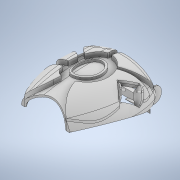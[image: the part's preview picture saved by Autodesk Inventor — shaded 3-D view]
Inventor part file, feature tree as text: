
AUTODESK INVENTOR PART (.ipt)
format: ipt  version: 2022 (Build 260153000, 153)  size: 2,761,216 bytes
history: native  units: mm
features: extrude x44, sketch x21, other x16, fillet x6, loft x1, shell x1, projected_geometry x1
ambient origin geometry x8: Origin, YZ Plane, XZ Plane, XY Plane, X Axis, Y Axis, Z Axis, Center Point
bodies: Body1 (feature_tree)
feature tree (90):
  other  "솔리드2"
  sketch  "스케치3"
  other  "작업 평면1"
  other  "작업 평면3"
  other  "작업 평면4"
  sketch  "스케치9"
  sketch  "스케치10"
  loft  "로프트1"
  shell  "쉘1"  Thickness=20.0mm
  fillet  "모깎기2"  [1 undecoded]
  extrude  "돌출3"  Depth=40.0mm
  extrude  "돌출5"  Depth=55.0mm
  extrude  "돌출6"  Depth=40.0mm
  sketch  "스케치21"
  sketch  "스케치22"
  sketch  "스케치23"
  sketch  "스케치24"
  extrude  "돌출9"  Depth=45.0mm
  extrude  "돌출10"  Depth=25.0mm
  extrude  "돌출11"  TaperAngle=0.0deg  [1 undecoded]
  fillet  "모깎기3"  [1 undecoded]
  other  "작업 평면9"
  sketch  "스케치28"
  other  "작업 평면11"
  extrude  "돌출12"  TaperAngle=0.0deg  [1 undecoded]
  fillet  "모깎기4"  Radius=5.0mm
  other  "작업 평면13"
  other  "작업 평면14"
  extrude  "돌출14"  Depth=110.605575mm
  extrude  "돌출15"  Depth=20.0mm
  sketch  "스케치32"
  extrude  "돌출16"  Depth=20.0mm
  extrude  "돌출17"  Depth=20.0mm
  fillet  "모깎기5"  Radius=20.0mm
  other  "작업 평면15"
  sketch  "스케치34"
  extrude  "돌출18"  Depth=20.0mm
  extrude  "돌출19"  Depth=1.677mm
  extrude  "돌출20"  Depth=1.677mm
  extrude  "돌출21"  Depth=1.677mm
  extrude  "돌출22"  Depth=1.677mm
  extrude  "돌출23"  Depth=88.385mm
  extrude  "돌출24"  Depth=44.1925mm
  extrude  "돌출25"  Depth=10.0mm
  extrude  "돌출26"  Depth=12.5mm
  extrude  "돌출27"  Depth=5.0mm TaperAngle=0.0deg
  extrude  "돌출28"  Depth=5.0mm TaperAngle=0.0deg
  sketch  "스케치35"
  sketch  "스케치36"
  extrude  "돌출29"  Depth=5.0mm TaperAngle=0.0deg
  extrude  "돌출30"  Depth=2.0mm
  other  "작업 평면16"
  sketch  "스케치37"
  extrude  "돌출31"  Depth=4.0mm TaperAngle=0.0deg
  extrude  "돌출32"  Depth=4.0mm TaperAngle=0.0deg
  extrude  "돌출33"  Depth=4.0mm TaperAngle=0.0deg
  extrude  "돌출34"  Depth=9.0mm
  extrude  "돌출35"  TaperAngle=0.0deg  [1 undecoded]
  extrude  "돌출36"  [1 undecoded]
  extrude  "돌출37"  Depth=50.0mm TaperAngle=0.0deg
  extrude  "돌출38"  Depth=2.0mm
  sketch  "스케치40"
  extrude  "돌출40"  Depth=30.0mm TaperAngle=30.0deg
  extrude  "돌출41"  Depth=6.108652mm
  extrude  "돌출42"  Depth=20.0mm
  other  "작업 평면17"
  sketch  "스케치42"
  extrude  "돌출43"  Depth=20.0mm
  extrude  "돌출44"  Depth=30.0mm TaperAngle=0.0deg
  extrude  "돌출45"  Depth=1.677mm
  extrude  "돌출46"  Depth=1.677mm
  other  "작업 평면18"
  extrude  "돌출47"  Depth=20.0mm TaperAngle=0.0deg
  extrude  "돌출48"  Depth=20.0mm
  extrude  "돌출49"  Depth=10.0mm
  extrude  "돌출50"  Depth=2.0mm
  fillet  "모깎기6"  Radius=2.0mm
  other  "작업 평면19"
  sketch  "스케치45"
  fillet  "모깎기7"  Radius=4.0mm
  extrude  "돌출57"  Depth=4.0mm TaperAngle=0.0deg
  other  "작업 평면2"
  other  "작업 평면10"
  sketch  "스케치29"
  other  "작업 평면12"
  sketch  "스케치33"
  sketch  "스케치41"
  sketch  "스케치43"
  sketch  "스케치44"
  projected_geometry  "투영된 루프2"
note: 6 required parameter values undecoded (feature->parameter linkage not recoverable at this tier; creation-order binding heuristic only, values carry confidence <= 0.55)
